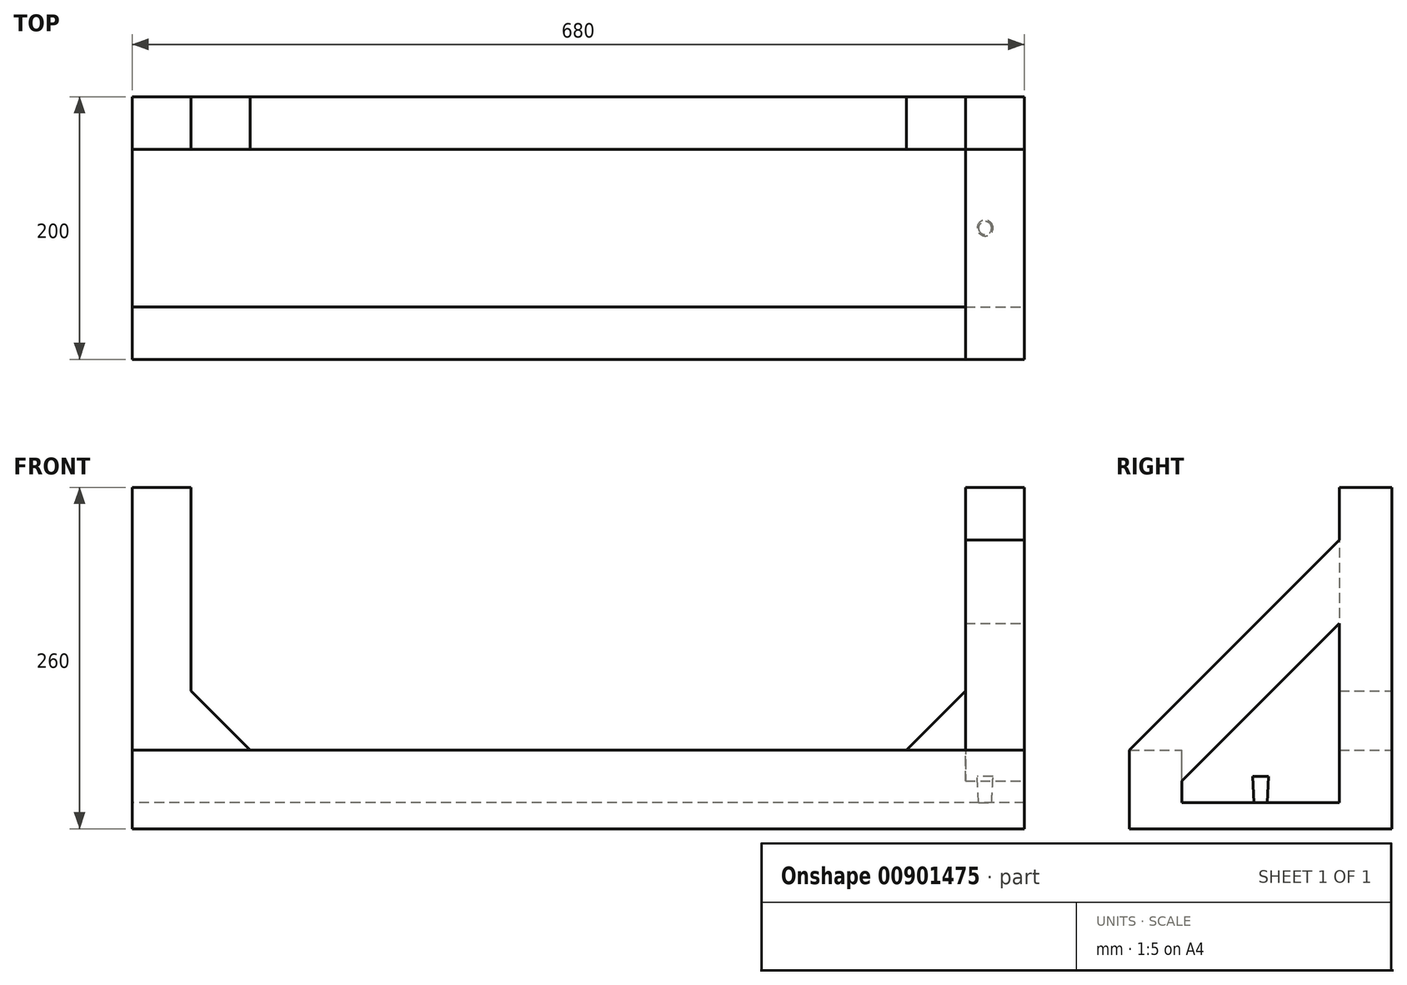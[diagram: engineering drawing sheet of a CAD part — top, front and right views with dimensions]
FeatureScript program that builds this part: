
annotation { "Feature Type Name" : "Feature", "Feature Type Description" : "" }
export const myFeature = defineFeature(function(context is Context, id is Id, definition is map)
    precondition{}
    {
        {
            var Q0;
            Q0=qCreatedBy(makeId("Right.planeOp"),FACE);
            var sketch = newSketch(context, id + "F0", { "sketchPlane" : qUnion([Q0])});
            skLineSegment(sketch, "E0.bottom", {"start": v(100, 10) * mm, "end": v(-100, 10) * mm});
            skLineSegment(sketch, "E0.top", {"start": v(100, -10) * mm, "end": v(-100, -10) * mm});
            skLineSegment(sketch, "E0.left", {"start": v(100, 10) * mm, "end": v(100, -10) * mm});
            skLineSegment(sketch, "E0.right", {"start": v(-100, 10) * mm, "end": v(-100, -10) * mm});
            skPoint(sketch, "E0.middle", {"position": v(0, 0) * mm});
            skSolve(sketch);
        }
        {
            var Q0;
            Q0 = qSketchRegion(id + "F0", true);
            extrude(context, id + "F1", {"entities" : qUnion([Q0]), "endBound" : BoundingType.SYMMETRIC, "depth" : 680 * mm, "offsetDistance" : 25 * mm});
        }
        {
            var Q0;
            Q0=qCreatedBy(makeId("Right.planeOp"),FACE);
            var sketch = newSketch(context, id + "F2", { "sketchPlane" : qUnion([Q0])});
            skLineSegment(sketch, "E1.bottom", {"start": v(-100, 10) * mm, "end": v(-60, 10) * mm});
            skLineSegment(sketch, "E1.top", {"start": v(-100, 50) * mm, "end": v(-60, 50) * mm});
            skLineSegment(sketch, "E1.left", {"start": v(-100, 10) * mm, "end": v(-100, 50) * mm});
            skLineSegment(sketch, "E1.right", {"start": v(-60, 10) * mm, "end": v(-60, 50) * mm});
            skLineSegment(sketch, "E2.bottom", {"start": v(60, 50) * mm, "end": v(100, 50) * mm});
            skLineSegment(sketch, "E2.top", {"start": v(60, 10) * mm, "end": v(100, 10) * mm});
            skLineSegment(sketch, "E2.left", {"start": v(60, 50) * mm, "end": v(60, 10) * mm});
            skLineSegment(sketch, "E2.right", {"start": v(100, 50) * mm, "end": v(100, 10) * mm});
            skSolve(sketch);
        }
        {
            var Q0;
            Q0=makeQuery(id+"F2.imprint","IMPRINT",FACE,{"disambiguationData":[TD([[makeQuery(id+"F2.imprint","IMPRINT",EDGE,{"derivedFrom":sQuery(id+"F2.wireOp",EDGE,"E2.bottom")}),-1.0]])]});
            var Q1;
            Q1=makeQuery(id+"F2.imprint","IMPRINT",FACE,{"disambiguationData":[TD([[makeQuery(id+"F2.imprint","IMPRINT",EDGE,{"derivedFrom":sQuery(id+"F2.wireOp",EDGE,"E1.bottom")}),1.0]])]});
            extrude(context, id + "F3", {"entities" : qUnion([Q0, Q1]), "operationType" : NewBodyOperationType.ADD, "endBound" : BoundingType.SYMMETRIC, "depth" : 680 * mm, "offsetDistance" : 25 * mm});
        }
        {
            var Q0;
            Q0=makeQuery(id+"F3.opExtrude","SWEPT_FACE",FACE,{"disambiguationData":[OSD([sQuery(id+"F2.wireOp",EDGE,"E2.bottom")])]});
            var sketch = newSketch(context, id + "F4", { "sketchPlane" : qUnion([Q0])});
            skLineSegment(sketch, "E3.bottom", {"start": v(-340, 100) * mm, "end": v(-295, 100) * mm});
            skLineSegment(sketch, "E3.top", {"start": v(-340, 60) * mm, "end": v(-295, 60) * mm});
            skLineSegment(sketch, "E3.left", {"start": v(-340, 100) * mm, "end": v(-340, 60) * mm});
            skLineSegment(sketch, "E3.right", {"start": v(-295, 100) * mm, "end": v(-295, 60) * mm});
            skLineSegment(sketch, "E4.bottom", {"start": v(340, 100) * mm, "end": v(295, 100) * mm});
            skLineSegment(sketch, "E4.top", {"start": v(340, 60) * mm, "end": v(295, 60) * mm});
            skLineSegment(sketch, "E4.left", {"start": v(340, 100) * mm, "end": v(340, 60) * mm});
            skLineSegment(sketch, "E4.right", {"start": v(295, 100) * mm, "end": v(295, 60) * mm});
            skSolve(sketch);
        }
        {
            var Q0;
            Q0 = qSketchRegion(id + "F4", true);
            extrude(context, id + "F5", {"entities" : qUnion([Q0]), "operationType" : NewBodyOperationType.ADD, "depth" : 200 * mm, "offsetDistance" : 25 * mm});
        }
        {
            var Q0;
            Q0=makeQuery(id+"F5.boolean.opBoolean","MERGE",FACE,{"derivedFrom":[makeQuery(id+"F3.boolean.opBoolean","MERGE",FACE,{"derivedFrom":[makeQuery(id+"F1.opExtrude","CAP_FACE",FACE,{"disambiguationData":[OSD([sQuery(id+"F0.wireOp",EDGE,"E0.bottom"),sQuery(id+"F0.wireOp",EDGE,"E0.top"),sQuery(id+"F0.wireOp",EDGE,"E0.left"),sQuery(id+"F0.wireOp",EDGE,"E0.right")])],"isStart":false}),makeQuery(id+"F3.opExtrude","CAP_FACE",FACE,{"disambiguationData":[OSD([sQuery(id+"F2.wireOp",EDGE,"E1.bottom"),sQuery(id+"F2.wireOp",EDGE,"E1.top"),sQuery(id+"F2.wireOp",EDGE,"E1.left"),sQuery(id+"F2.wireOp",EDGE,"E1.right")])],"isStart":false}),makeQuery(id+"F3.opExtrude","CAP_FACE",FACE,{"disambiguationData":[OSD([sQuery(id+"F2.wireOp",EDGE,"E2.bottom"),sQuery(id+"F2.wireOp",EDGE,"E2.top"),sQuery(id+"F2.wireOp",EDGE,"E2.left"),sQuery(id+"F2.wireOp",EDGE,"E2.right")])],"isStart":false})]}),makeQuery(id+"F5.opExtrude","SWEPT_FACE",FACE,{"disambiguationData":[OSD([sQuery(id+"F4.wireOp",EDGE,"E4.left")])]})]});
            var sketch = newSketch(context, id + "F6", { "sketchPlane" : qUnion([Q0])});
            skLineSegment(sketch, "E5", {"start": v(-100, 50) * mm, "end": v(60, 210) * mm});
            skLineSegment(sketch, "E6", {"start": v(60, 210) * mm, "end": v(60, 146.36) * mm});
            skLineSegment(sketch, "E7", {"start": v(60, 146.36) * mm, "end": v(-60, 26.36) * mm});
            skLineSegment(sketch, "E8", {"start": v(-60, 26.36) * mm, "end": v(-60, 50) * mm});
            skLineSegment(sketch, "E9", {"start": v(-60, 50) * mm, "end": v(-100, 50) * mm});
            skSolve(sketch);
        }
        {
            var Q0;
            Q0 = qSketchRegion(id + "F6", true);
            extrude(context, id + "F7", {"entities" : qUnion([Q0]), "operationType" : NewBodyOperationType.ADD, "oppositeDirection" : true, "depth" : 45 * mm, "offsetDistance" : 25 * mm});
        }
        {
            var Q0;
            Q0=makeQuery(id+"F5.boolean.opBoolean","MERGE",FACE,{"derivedFrom":[makeQuery(id+"F3.boolean.opBoolean","MERGE",FACE,{"derivedFrom":[makeQuery(id+"F1.opExtrude","SWEPT_FACE",FACE,{"disambiguationData":[OSD([sQuery(id+"F0.wireOp",EDGE,"E0.left")])]}),makeQuery(id+"F3.opExtrude","SWEPT_FACE",FACE,{"disambiguationData":[OSD([sQuery(id+"F2.wireOp",EDGE,"E2.right")])]})]}),makeQuery(id+"F5.opExtrude","SWEPT_FACE",FACE,{"disambiguationData":[OSD([sQuery(id+"F4.wireOp",EDGE,"E3.bottom")])]}),makeQuery(id+"F5.opExtrude","SWEPT_FACE",FACE,{"disambiguationData":[OSD([sQuery(id+"F4.wireOp",EDGE,"E4.bottom")])]})]});
            var sketch = newSketch(context, id + "F8", { "sketchPlane" : qUnion([Q0])});
            skLineSegment(sketch, "E10", {"start": v(-295, 95) * mm, "end": v(-250, 50) * mm});
            skLineSegment(sketch, "E11", {"start": v(-250, 50) * mm, "end": v(-295, 50) * mm});
            skLineSegment(sketch, "E12", {"start": v(-295, 50) * mm, "end": v(-295, 95) * mm});
            skLineSegment(sketch, "E13", {"start": v(295, 95) * mm, "end": v(295, 50) * mm});
            skLineSegment(sketch, "E14", {"start": v(295, 50) * mm, "end": v(250, 50) * mm});
            skLineSegment(sketch, "E15", {"start": v(250, 50) * mm, "end": v(295, 95) * mm});
            skSolve(sketch);
        }
        {
            var Q0;
            Q0 = qSketchRegion(id + "F8", true);
            extrude(context, id + "F9", {"entities" : qUnion([Q0]), "operationType" : NewBodyOperationType.ADD, "oppositeDirection" : true, "depth" : 40 * mm, "offsetDistance" : 25 * mm});
        }
        {
            var Q0;
            Q0=makeQuery(id+"F1.opExtrude","SWEPT_FACE",FACE,{"disambiguationData":[OSD([sQuery(id+"F0.wireOp",EDGE,"E0.bottom")])]});
            var sketch = newSketch(context, id + "F10", { "sketchPlane" : qUnion([Q0])});
            skCircle(sketch, "E16", {"center": v(310, 0) * mm, "radius": 5 * mm});
            skSolve(sketch);
        }
        {
            var Q0;
            Q0 = qSketchRegion(id + "F10", true);
            extrude(context, id + "F11", {"entities" : qUnion([Q0]), "operationType" : NewBodyOperationType.ADD, "depth" : 20 * mm, "offsetDistance" : 25 * mm, "hasDraft" : true, "draftAngle" : 3 * degree});
        }
    });
